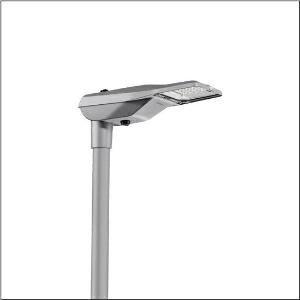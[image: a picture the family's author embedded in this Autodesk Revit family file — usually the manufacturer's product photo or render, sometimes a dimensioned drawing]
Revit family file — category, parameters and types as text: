
# Revit family: streetlight_sl_21_iq_micro___st0_8a_5xe1c31y08cb_ba99
name_source: partatom
category: Lighting Fixtures
units: mm (PartAtom-declared; Revit-internal decimal feet)

## family parameters
Cut with Voids When Loaded = No
Host = Face
Light Source = No
Part Type = Normal
Room Calculation Point = No
Round Connector Dimension = Use Diameter
Shared = No

## types (1)
- --- (1 x LED, 2880 lm, 19.1 W, 3000K)
    Apparent Load = 19 VA
    CIE Flux Codes = 38 75 97 100 100
    Color Rendering = 70
    Color Temperature = 3000K
    Default Elevation = 1800 mm
    Description = Streetlight SL 21 iQ micro, mast luminaire, primary light control with lens, of PMMA, primary optical cover: cover, of toughened safety glass, transparent, light distribution: ST0.8a, light emission: direct distribution, primary light characteristic: asymmetric, installation type: post-top, side-entry, LED, High Power LED, rated luminous flux: 2.880lm, luminous efficacy: 151lm/W, light colour: 730, colour temperature: 3000K, control: pre-setting: logarithmic dimming characteristic, Street-Remote, Auto-Match, Temp-Guard, Lumen-Switch, Night-Set, Smart-Wire, Light-Fading, Desk-Remote (wireless, voltage-free reading and setting of iQ features in the workshop via application-optimized NFC function/RFID function), optimised constant luminous flux control (CLO 2.0), mains connection: 220..240V, AC, 50/60Hz, start of lifetime: 19W, end of service life: 20W, reduction: 9W, luminaire housing, of diecast aluminium, powder-coated, Siteco® metallic grey (DB 702S), corrosivity category C5 mid according to DIN EN ISO 12944, please order mast flange separately, inclination adjustable: 0°, 5°, 10°, 15°, sealing non-destructively replaceable, multi-level sealing system, length: 528mm, width: 235mm, height: 110mm, mast flange for spigot size: 42mm (side-entry): 5XC10008XM4, 60/48mm (side-entry/post-top): 5XC10108XM2, 76/60mm (side-entry/post-top): 5XC10108XM1, Smart Interface below and above, protection rating (complete): IP66, insulation class (complete): insulation class II (safety insulation), certification: CE, ENEC, ENEC+, VDE, impact resistance: IK09, permissible operating ambient temperature for outdoor applications: -40..+50°C, standard-compliant lighting for roads and squares, packaging unit: 1 piece

Light Distribution: ST0.8a
    Height = 110 mm
    Lamp = 1 x LED
    Lamp Light Flux = 2880 lm
    Lamp Power = 19.1 W
    Lamp count = 1
    Length = 528 mm
    Luminous efficacy = 151 lm/W
    Manufacturer = Siteco
    ModVariant = No
    Model = 5XE1C31Y08CB
    Number of Poles = 1
    OnlyDefault = Yes
    Power Factor = 1
    Product Name = Streetlight SL 21 iQ micro | ST0.8a
    Product group = mast luminaire | pylon top
    ProductGroupID = 6100
    Protection Class = Protection class II
    Protection Degree = IP 66
    RLX_Detail_Level = 1
    RLX_Emergency_Light_Flux = 0 lm
    RLX_Emergency_Type = 0
    RLX_Emergency_Type_DB = No
    RlxData = <blob elided: 99325 chars, md5=ec4f1773>
    Socket = socket
    Standby Power = 0 W
    System Light Flux = 2880 lm
    System Power = 19 W
    Type Comments = factory setting: luminous flux: 100 % | dim-lin: 254 | 387 mA
    Type Image = l_1007239.jpg
    URL = http://relux.com
    VarID = @adj_082271
    Voltage = 0 V
    Weight = 0.00 kg
    Width = 235 mm

## geometry (parser evidence)
native form markers: Blend x4, Sweep x11
no freeform markers — native parametric forms only
